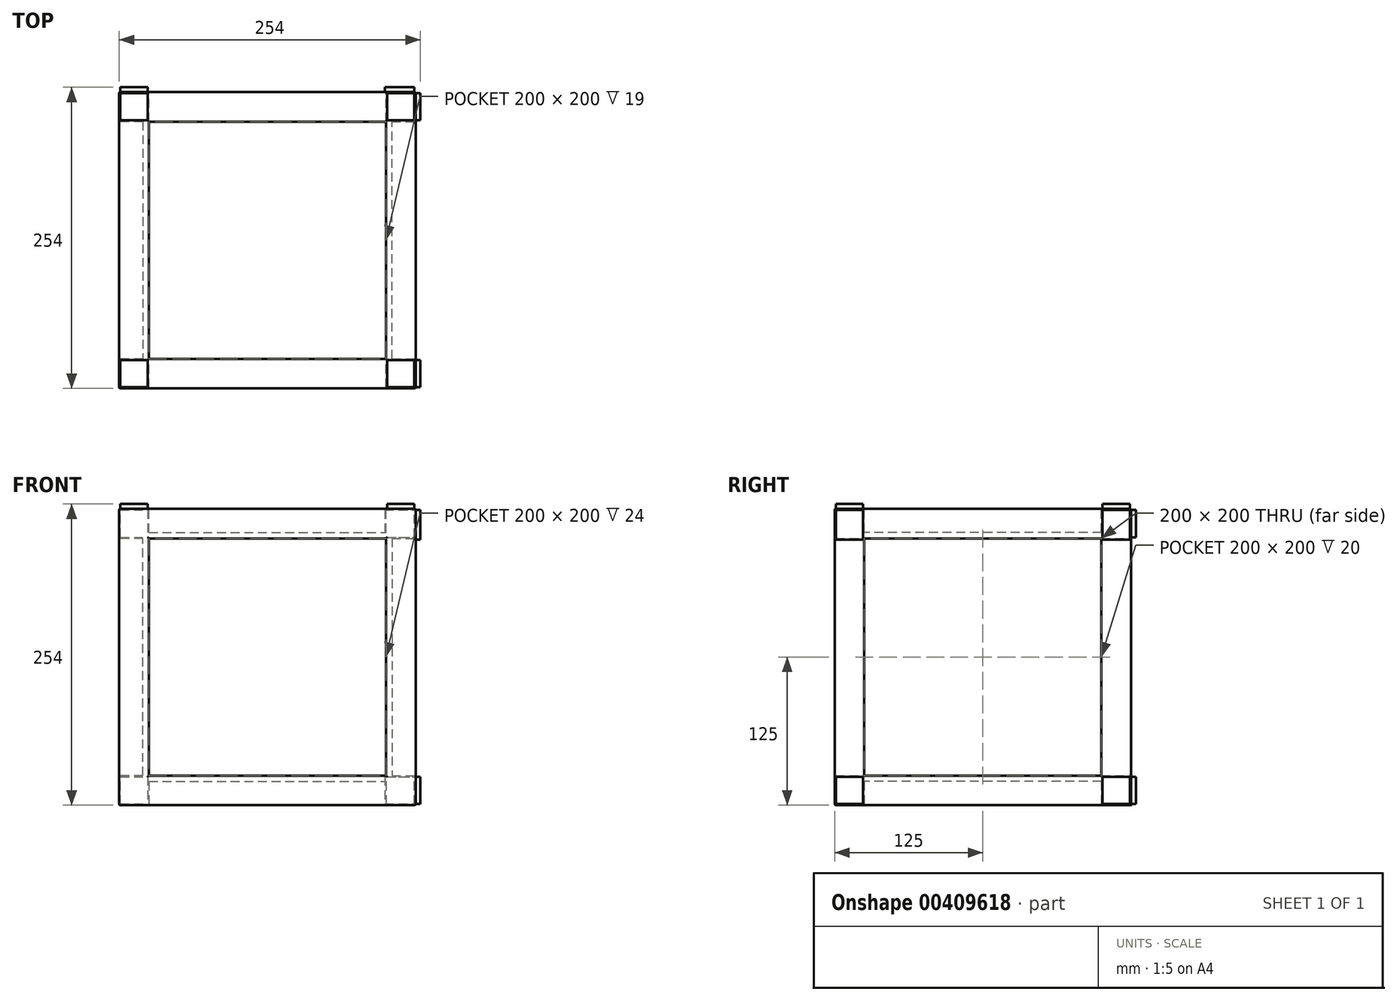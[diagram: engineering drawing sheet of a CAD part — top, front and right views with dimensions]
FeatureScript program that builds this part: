
annotation { "Feature Type Name" : "Feature", "Feature Type Description" : "" }
export const myFeature = defineFeature(function(context is Context, id is Id, definition is map)
    precondition{}
    {
        {
            var Q0;
            Q0=qCreatedBy(makeId("Front.planeOp"),FACE);
            var sketch = newSketch(context, id + "F0", { "sketchPlane" : qUnion([Q0])});
            skLineSegment(sketch, "E0.bottom", {"start": v(0, 0) * mm, "end": v(250, 0) * mm});
            skLineSegment(sketch, "E0.top", {"start": v(0, 250) * mm, "end": v(250, 250) * mm});
            skLineSegment(sketch, "E0.left", {"start": v(0, 0) * mm, "end": v(0, 250) * mm});
            skLineSegment(sketch, "E0.right", {"start": v(250, 0) * mm, "end": v(250, 250) * mm});
            skLineSegment(sketch, "E1.bottom", {"start": v(25, 225) * mm, "end": v(225, 225) * mm});
            skLineSegment(sketch, "E1.top", {"start": v(25, 25) * mm, "end": v(225, 25) * mm});
            skLineSegment(sketch, "E1.left", {"start": v(25, 225) * mm, "end": v(25, 25) * mm});
            skLineSegment(sketch, "E1.right", {"start": v(225, 225) * mm, "end": v(225, 25) * mm});
            skSolve(sketch);
        }
        {
            var Q0;
            Q0=makeQuery(id+"F0.imprint","IMPRINT",FACE,{"disambiguationData":[TD([[makeQuery(id+"F0.imprint","IMPRINT",EDGE,{"derivedFrom":sQuery(id+"F0.wireOp",EDGE,"E0.bottom")}),1.0]])]});
            extrude(context, id + "F1", {"entities" : qUnion([Q0]), "endBound" : BoundingType.SYMMETRIC, "depth" : 250 * mm});
        }
        {
            var Q0;
            Q0=qCreatedBy(makeId("Front.planeOp"),FACE);
            var sketch = newSketch(context, id + "F2", { "sketchPlane" : qUnion([Q0])});
            skLineSegment(sketch, "E2.bottom", {"start": v(25, 25) * mm, "end": v(225, 25) * mm});
            skLineSegment(sketch, "E2.top", {"start": v(25, 225) * mm, "end": v(225, 225) * mm});
            skLineSegment(sketch, "E2.left", {"start": v(25, 25) * mm, "end": v(25, 225) * mm});
            skLineSegment(sketch, "E2.right", {"start": v(225, 25) * mm, "end": v(225, 225) * mm});
            skSolve(sketch);
        }
        {
            var Q0;
            Q0=makeQuery(id+"F2.imprint","IMPRINT",FACE,{"disambiguationData":[TD([[makeQuery(id+"F2.imprint","IMPRINT",EDGE,{"derivedFrom":sQuery(id+"F2.wireOp",EDGE,"E2.bottom")}),1.0]])]});
            extrude(context, id + "F3", {"entities" : qUnion([Q0]), "operationType" : NewBodyOperationType.ADD, "endBound" : BoundingType.SYMMETRIC, "depth" : 200 * mm});
        }
        {
            var Q0;
            Q0=makeQuery(id+"F1.opExtrude","SWEPT_FACE",FACE,{"disambiguationData":[OSD([sQuery(id+"F0.wireOp",EDGE,"E0.left")])]});
            var sketch = newSketch(context, id + "F4", { "sketchPlane" : qUnion([Q0])});
            skLineSegment(sketch, "E3.bottom", {"start": v(-100, 25) * mm, "end": v(100, 25) * mm});
            skLineSegment(sketch, "E3.top", {"start": v(-100, 225) * mm, "end": v(100, 225) * mm});
            skLineSegment(sketch, "E3.left", {"start": v(-100, 25) * mm, "end": v(-100, 225) * mm});
            skLineSegment(sketch, "E3.right", {"start": v(100, 25) * mm, "end": v(100, 225) * mm});
            skSolve(sketch);
        }
        {
            var Q0;
            Q0=makeQuery(id+"F4.imprint","IMPRINT",FACE,{"disambiguationData":[TD([[makeQuery(id+"F4.imprint","IMPRINT",EDGE,{"derivedFrom":sQuery(id+"F4.wireOp",EDGE,"E3.bottom")}),1.0]])]});
            extrude(context, id + "F5", {"entities" : qUnion([Q0]), "operationType" : NewBodyOperationType.REMOVE, "oppositeDirection" : true, "depth" : 20 * mm});
        }
        {
            var Q0;
            Q0=makeQuery(id+"F1.opExtrude","SWEPT_FACE",FACE,{"disambiguationData":[OSD([sQuery(id+"F0.wireOp",EDGE,"E0.right")])]});
            var sketch = newSketch(context, id + "F6", { "sketchPlane" : qUnion([Q0])});
            skLineSegment(sketch, "E4.bottom", {"start": v(-100, 225) * mm, "end": v(100, 225) * mm});
            skLineSegment(sketch, "E4.top", {"start": v(-100, 25) * mm, "end": v(100, 25) * mm});
            skLineSegment(sketch, "E4.left", {"start": v(-100, 225) * mm, "end": v(-100, 25) * mm});
            skLineSegment(sketch, "E4.right", {"start": v(100, 225) * mm, "end": v(100, 25) * mm});
            skSolve(sketch);
        }
        {
            var Q0;
            Q0=makeQuery(id+"F6.imprint","IMPRINT",FACE,{"disambiguationData":[TD([[makeQuery(id+"F6.imprint","IMPRINT",EDGE,{"derivedFrom":sQuery(id+"F6.wireOp",EDGE,"E4.bottom")}),-1.0]])]});
            extrude(context, id + "F7", {"entities" : qUnion([Q0]), "operationType" : NewBodyOperationType.REMOVE, "oppositeDirection" : true, "depth" : 20 * mm});
        }
        {
            var Q0;
            Q0=qCreatedBy(makeId("Top.planeOp"),FACE);
            var sketch = newSketch(context, id + "F8", { "sketchPlane" : qUnion([Q0])});
            skLineSegment(sketch, "E5.bottom", {"start": v(25, 100) * mm, "end": v(225, 100) * mm});
            skLineSegment(sketch, "E5.top", {"start": v(25, -100) * mm, "end": v(225, -100) * mm});
            skLineSegment(sketch, "E5.left", {"start": v(25, 100) * mm, "end": v(25, -100) * mm});
            skLineSegment(sketch, "E5.right", {"start": v(225, 100) * mm, "end": v(225, -100) * mm});
            skSolve(sketch);
        }
        {
            var Q0;
            Q0=makeQuery(id+"F8.imprint","IMPRINT",FACE,{"disambiguationData":[TD([[makeQuery(id+"F8.imprint","IMPRINT",EDGE,{"derivedFrom":sQuery(id+"F8.wireOp",EDGE,"E5.bottom")}),-1.0]])]});
            extrude(context, id + "F9", {"entities" : qUnion([Q0]), "operationType" : NewBodyOperationType.REMOVE, "depth" : 20 * mm});
        }
        {
            var Q0;
            Q0=makeQuery(id+"F1.opExtrude","SWEPT_FACE",FACE,{"disambiguationData":[OSD([sQuery(id+"F0.wireOp",EDGE,"E0.top")])]});
            var sketch = newSketch(context, id + "F10", { "sketchPlane" : qUnion([Q0])});
            skLineSegment(sketch, "E6.bottom", {"start": v(25, 100) * mm, "end": v(225, 100) * mm});
            skLineSegment(sketch, "E6.top", {"start": v(25, -100) * mm, "end": v(225, -100) * mm});
            skLineSegment(sketch, "E6.left", {"start": v(25, 100) * mm, "end": v(25, -100) * mm});
            skLineSegment(sketch, "E6.right", {"start": v(225, 100) * mm, "end": v(225, -100) * mm});
            skSolve(sketch);
        }
        {
            var Q0;
            Q0=makeQuery(id+"F10.imprint","IMPRINT",FACE,{"disambiguationData":[TD([[makeQuery(id+"F10.imprint","IMPRINT",EDGE,{"derivedFrom":sQuery(id+"F10.wireOp",EDGE,"E6.bottom")}),-1.0]])]});
            extrude(context, id + "F11", {"entities" : qUnion([Q0]), "operationType" : NewBodyOperationType.REMOVE, "oppositeDirection" : true, "depth" : 20 * mm});
        }
        {
            var Q0;
            Q0=makeQuery(id+"F9.boolean.opBoolean","COPY",EDGE,{"derivedFrom":makeQuery(id+"F9.opExtrude","CAP_EDGE",EDGE,{"disambiguationData":[OSD([sQuery(id+"F8.wireOp",EDGE,"E5.left")])],"isStart":true})});
            var Q1;
            Q1=makeQuery(id+"F9.boolean.opBoolean","COPY",EDGE,{"derivedFrom":makeQuery(id+"F9.opExtrude","CAP_EDGE",EDGE,{"disambiguationData":[OSD([sQuery(id+"F8.wireOp",EDGE,"E5.top")])],"isStart":true})});
            var Q2;
            Q2=makeQuery(id+"F9.boolean.opBoolean","COPY",EDGE,{"derivedFrom":makeQuery(id+"F9.opExtrude","CAP_EDGE",EDGE,{"disambiguationData":[OSD([sQuery(id+"F8.wireOp",EDGE,"E5.bottom")])],"isStart":true})});
            var Q3;
            Q3=makeQuery(id+"F9.boolean.opBoolean","COPY",EDGE,{"derivedFrom":makeQuery(id+"F9.opExtrude","CAP_EDGE",EDGE,{"disambiguationData":[OSD([sQuery(id+"F8.wireOp",EDGE,"E5.right")])],"isStart":true})});
            var Q4;
            Q4=makeQuery(id+"F1.opExtrude","SWEPT_EDGE",EDGE,{"disambiguationData":[OSD([sQuery(id+"F0.wireOp",EDGE,"E0.bottom"),sQuery(id+"F0.wireOp",EDGE,"E0.right")])]});
            var Q5;
            Q5=makeQuery(id+"F7.boolean.opBoolean","COPY",EDGE,{"derivedFrom":makeQuery(id+"F7.opExtrude","CAP_EDGE",EDGE,{"disambiguationData":[OSD([sQuery(id+"F6.wireOp",EDGE,"E4.top")])],"isStart":true})});
            var Q6;
            Q6=makeQuery(id+"F7.boolean.opBoolean","COPY",EDGE,{"derivedFrom":makeQuery(id+"F7.opExtrude","CAP_EDGE",EDGE,{"disambiguationData":[OSD([sQuery(id+"F6.wireOp",EDGE,"E4.right")])],"isStart":true})});
            var Q7;
            Q7=makeQuery(id+"F7.boolean.opBoolean","COPY",EDGE,{"derivedFrom":makeQuery(id+"F7.opExtrude","CAP_EDGE",EDGE,{"disambiguationData":[OSD([sQuery(id+"F6.wireOp",EDGE,"E4.bottom")])],"isStart":true})});
            var Q8;
            Q8=makeQuery(id+"F7.boolean.opBoolean","COPY",EDGE,{"derivedFrom":makeQuery(id+"F7.opExtrude","CAP_EDGE",EDGE,{"disambiguationData":[OSD([sQuery(id+"F6.wireOp",EDGE,"E4.left")])],"isStart":true})});
            var Q9;
            Q9=makeQuery(id+"F1.opExtrude","CAP_EDGE",EDGE,{"disambiguationData":[OSD([sQuery(id+"F0.wireOp",EDGE,"E0.right")])],"isStart":false});
            var Q10;
            Q10=makeQuery(id+"F1.opExtrude","SWEPT_EDGE",EDGE,{"disambiguationData":[OSD([sQuery(id+"F0.wireOp",EDGE,"E0.top"),sQuery(id+"F0.wireOp",EDGE,"E0.right")])]});
            var Q11;
            Q11=makeQuery(id+"F1.opExtrude","CAP_EDGE",EDGE,{"disambiguationData":[OSD([sQuery(id+"F0.wireOp",EDGE,"E0.top")])],"isStart":true});
            var Q12;
            Q12=makeQuery(id+"F1.opExtrude","CAP_EDGE",EDGE,{"disambiguationData":[OSD([sQuery(id+"F0.wireOp",EDGE,"E0.right")])],"isStart":true});
            var Q13;
            Q13=makeQuery(id+"F1.opExtrude","CAP_EDGE",EDGE,{"disambiguationData":[OSD([sQuery(id+"F0.wireOp",EDGE,"E1.right")])],"isStart":true});
            var Q14;
            Q14=makeQuery(id+"F1.opExtrude","CAP_EDGE",EDGE,{"disambiguationData":[OSD([sQuery(id+"F0.wireOp",EDGE,"E1.bottom")])],"isStart":true});
            var Q15;
            Q15=makeQuery(id+"F1.opExtrude","CAP_EDGE",EDGE,{"disambiguationData":[OSD([sQuery(id+"F0.wireOp",EDGE,"E1.left")])],"isStart":true});
            var Q16;
            Q16=makeQuery(id+"F1.opExtrude","CAP_EDGE",EDGE,{"disambiguationData":[OSD([sQuery(id+"F0.wireOp",EDGE,"E1.top")])],"isStart":true});
            var Q17;
            Q17=makeQuery(id+"F5.boolean.opBoolean","COPY",EDGE,{"derivedFrom":makeQuery(id+"F5.opExtrude","CAP_EDGE",EDGE,{"disambiguationData":[OSD([sQuery(id+"F4.wireOp",EDGE,"E3.left")])],"isStart":true})});
            var Q18;
            Q18=makeQuery(id+"F5.boolean.opBoolean","COPY",EDGE,{"derivedFrom":makeQuery(id+"F5.opExtrude","CAP_EDGE",EDGE,{"disambiguationData":[OSD([sQuery(id+"F4.wireOp",EDGE,"E3.bottom")])],"isStart":true})});
            var Q19;
            Q19=makeQuery(id+"F1.opExtrude","CAP_EDGE",EDGE,{"disambiguationData":[OSD([sQuery(id+"F0.wireOp",EDGE,"E0.left")])],"isStart":true});
            var Q20;
            Q20=makeQuery(id+"F1.opExtrude","SWEPT_EDGE",EDGE,{"disambiguationData":[OSD([sQuery(id+"F0.wireOp",EDGE,"E0.bottom"),sQuery(id+"F0.wireOp",EDGE,"E0.left")])]});
            var Q21;
            Q21=makeQuery(id+"F1.opExtrude","CAP_EDGE",EDGE,{"disambiguationData":[OSD([sQuery(id+"F0.wireOp",EDGE,"E0.left")])],"isStart":false});
            var Q22;
            Q22=makeQuery(id+"F1.opExtrude","SWEPT_EDGE",EDGE,{"disambiguationData":[OSD([sQuery(id+"F0.wireOp",EDGE,"E0.top"),sQuery(id+"F0.wireOp",EDGE,"E0.left")])]});
            var Q23;
            Q23=makeQuery(id+"F5.boolean.opBoolean","COPY",EDGE,{"derivedFrom":makeQuery(id+"F5.opExtrude","CAP_EDGE",EDGE,{"disambiguationData":[OSD([sQuery(id+"F4.wireOp",EDGE,"E3.top")])],"isStart":true})});
            var Q24;
            Q24=makeQuery(id+"F5.boolean.opBoolean","COPY",EDGE,{"derivedFrom":makeQuery(id+"F5.opExtrude","CAP_EDGE",EDGE,{"disambiguationData":[OSD([sQuery(id+"F4.wireOp",EDGE,"E3.right")])],"isStart":true})});
            var Q25;
            Q25=makeQuery(id+"F1.opExtrude","CAP_EDGE",EDGE,{"disambiguationData":[OSD([sQuery(id+"F0.wireOp",EDGE,"E0.top")])],"isStart":false});
            var Q26;
            Q26=makeQuery(id+"F1.opExtrude","CAP_FACE",FACE,{"disambiguationData":[OSD([sQuery(id+"F0.wireOp",EDGE,"E0.bottom"),sQuery(id+"F0.wireOp",EDGE,"E0.top"),sQuery(id+"F0.wireOp",EDGE,"E0.left"),sQuery(id+"F0.wireOp",EDGE,"E0.right"),sQuery(id+"F0.wireOp",EDGE,"E1.bottom"),sQuery(id+"F0.wireOp",EDGE,"E1.top"),sQuery(id+"F0.wireOp",EDGE,"E1.left"),sQuery(id+"F0.wireOp",EDGE,"E1.right")])],"isStart":false});
            var Q27;
            Q27=makeQuery(id+"F1.opExtrude","SWEPT_FACE",FACE,{"disambiguationData":[OSD([sQuery(id+"F0.wireOp",EDGE,"E0.top")])]});
            fillet(context, id + "F12", {"entities" : qUnion([Q0, Q1, Q2, Q3, Q4, Q5, Q6, Q7, Q8, Q9, Q10, Q11, Q12, Q13, Q14, Q15, Q16, Q17, Q18, Q19, Q20, Q21, Q22, Q23, Q24, Q25, Q26, Q27]), "radius" : 1 * mm, "tangentPropagation" : true, "allowEdgeOverflow" : false});
        }
        {
            var Q0;
            Q0=makeQuery(id+"F1.opExtrude","SWEPT_FACE",FACE,{"disambiguationData":[OSD([sQuery(id+"F0.wireOp",EDGE,"E0.top")])]});
            var sketch = newSketch(context, id + "F13", { "sketchPlane" : qUnion([Q0])});
            skLineSegment(sketch, "E7.bottom", {"start": v(249, 124) * mm, "end": v(226, 124) * mm});
            skLineSegment(sketch, "E7.top", {"start": v(249, 101) * mm, "end": v(226, 101) * mm});
            skLineSegment(sketch, "E7.left", {"start": v(249, 124) * mm, "end": v(249, 101) * mm});
            skLineSegment(sketch, "E7.right", {"start": v(226, 124) * mm, "end": v(226, 101) * mm});
            skLineSegment(sketch, "E8.0.1.0", {"start": v(249, -101) * mm, "end": v(249, -124) * mm});
            skLineSegment(sketch, "E8.0.1.1", {"start": v(249, -124) * mm, "end": v(226, -124) * mm});
            skLineSegment(sketch, "E8.0.1.2", {"start": v(226, -101) * mm, "end": v(226, -124) * mm});
            skLineSegment(sketch, "E8.0.1.3", {"start": v(249, -101) * mm, "end": v(226, -101) * mm});
            skLineSegment(sketch, "E8.1.0.0", {"start": v(24, 124) * mm, "end": v(24, 101) * mm});
            skLineSegment(sketch, "E8.1.0.1", {"start": v(24, 101) * mm, "end": v(1, 101) * mm});
            skLineSegment(sketch, "E8.1.0.2", {"start": v(1, 124) * mm, "end": v(1, 101) * mm});
            skLineSegment(sketch, "E8.1.0.3", {"start": v(24, 124) * mm, "end": v(1, 124) * mm});
            skLineSegment(sketch, "E8.1.1.0", {"start": v(24, -101) * mm, "end": v(24, -124) * mm});
            skLineSegment(sketch, "E8.1.1.1", {"start": v(24, -124) * mm, "end": v(1, -124) * mm});
            skLineSegment(sketch, "E8.1.1.2", {"start": v(1, -101) * mm, "end": v(1, -124) * mm});
            skLineSegment(sketch, "E8.1.1.3", {"start": v(24, -101) * mm, "end": v(1, -101) * mm});
            skLineSegment(sketch, "E8.direction1", {"start": v(249, 101) * mm, "end": v(24, 101) * mm, "construction": true});
            skLineSegment(sketch, "E8.direction2", {"start": v(249, 101) * mm, "end": v(249, -124) * mm, "construction": true});
            skSolve(sketch);
        }
        {
            var Q0;
            Q0=makeQuery(id+"F13.imprint","IMPRINT",FACE,{"disambiguationData":[TD([[makeQuery(id+"F13.imprint","IMPRINT",EDGE,{"derivedFrom":sQuery(id+"F13.wireOp",EDGE,"E7.bottom")}),1.0]])]});
            var Q1;
            Q1=makeQuery(id+"F13.imprint","IMPRINT",FACE,{"disambiguationData":[TD([[makeQuery(id+"F13.imprint","IMPRINT",EDGE,{"derivedFrom":sQuery(id+"F13.wireOp",EDGE,"E8.0.1.0")}),1.0]])]});
            var Q2;
            Q2=makeQuery(id+"F13.imprint","IMPRINT",FACE,{"disambiguationData":[TD([[makeQuery(id+"F13.imprint","IMPRINT",EDGE,{"derivedFrom":sQuery(id+"F13.wireOp",EDGE,"E8.1.1.0")}),-1.0]])]});
            var Q3;
            Q3=makeQuery(id+"F13.imprint","IMPRINT",FACE,{"disambiguationData":[TD([[makeQuery(id+"F13.imprint","IMPRINT",EDGE,{"derivedFrom":sQuery(id+"F13.wireOp",EDGE,"E8.1.0.0")}),-1.0]])]});
            extrude(context, id + "F14", {"entities" : qUnion([Q0, Q1, Q2, Q3]), "operationType" : NewBodyOperationType.ADD, "depth" : 4 * mm});
        }
        {
            var Q0;
            Q0=makeQuery(id+"F1.opExtrude","SWEPT_FACE",FACE,{"disambiguationData":[OSD([sQuery(id+"F0.wireOp",EDGE,"E0.right")])]});
            var sketch = newSketch(context, id + "F15", { "sketchPlane" : qUnion([Q0])});
            skLineSegment(sketch, "E9.bottom", {"start": v(124, 249) * mm, "end": v(101, 249) * mm});
            skLineSegment(sketch, "E9.top", {"start": v(124, 224) * mm, "end": v(101, 224) * mm});
            skLineSegment(sketch, "E9.left", {"start": v(124, 249) * mm, "end": v(124, 224) * mm});
            skLineSegment(sketch, "E9.right", {"start": v(101, 249) * mm, "end": v(101, 224) * mm});
            skLineSegment(sketch, "E10.0.1.0", {"start": v(124, 24) * mm, "end": v(124, -1) * mm});
            skLineSegment(sketch, "E10.0.1.1", {"start": v(124, -1) * mm, "end": v(101, -1) * mm});
            skLineSegment(sketch, "E10.0.1.2", {"start": v(101, 24) * mm, "end": v(101, -1) * mm});
            skLineSegment(sketch, "E10.0.1.3", {"start": v(124, 24) * mm, "end": v(101, 24) * mm});
            skLineSegment(sketch, "E10.1.0.0", {"start": v(-101, 249) * mm, "end": v(-101, 224) * mm});
            skLineSegment(sketch, "E10.1.0.1", {"start": v(-101, 224) * mm, "end": v(-124, 224) * mm});
            skLineSegment(sketch, "E10.1.0.2", {"start": v(-124, 249) * mm, "end": v(-124, 224) * mm});
            skLineSegment(sketch, "E10.1.0.3", {"start": v(-101, 249) * mm, "end": v(-124, 249) * mm});
            skLineSegment(sketch, "E10.1.1.0", {"start": v(-101, 24) * mm, "end": v(-101, -1) * mm});
            skLineSegment(sketch, "E10.1.1.1", {"start": v(-101, -1) * mm, "end": v(-124, -1) * mm});
            skLineSegment(sketch, "E10.1.1.2", {"start": v(-124, 24) * mm, "end": v(-124, -1) * mm});
            skLineSegment(sketch, "E10.1.1.3", {"start": v(-101, 24) * mm, "end": v(-124, 24) * mm});
            skLineSegment(sketch, "E10.direction1", {"start": v(124, 224) * mm, "end": v(-101, 224) * mm, "construction": true});
            skLineSegment(sketch, "E10.direction2", {"start": v(124, 224) * mm, "end": v(124, -1) * mm, "construction": true});
            skSolve(sketch);
        }
        {
            var Q0;
            {var subQ5=sQuery(id+"F15.wireOp",EDGE,"E9.bottom");Q0=makeQuery(id+"F15.imprint","IMPRINT",FACE,{"disambiguationData":[TD([[makeQuery(id+"F15.imprint","IMPRINT",EDGE,{"derivedFrom":subQ5}),1.0]])]});}
            var Q1;
            {var subQ0=sQuery(id+"F15.wireOp",EDGE,"E10.1.0.1");Q1=makeQuery(id+"F15.imprint","IMPRINT",FACE,{"disambiguationData":[TD([[makeQuery(id+"F15.imprint","IMPRINT",EDGE,{"derivedFrom":subQ0}),-1.0]])]});}
            var Q2;
            {var subQ0=sQuery(id+"F15.wireOp",EDGE,"E10.1.1.3");Q2=makeQuery(id+"F15.imprint","IMPRINT",FACE,{"disambiguationData":[TD([[makeQuery(id+"F15.imprint","IMPRINT",EDGE,{"derivedFrom":subQ0}),1.0]])]});}
            var Q3;
            {var subQ5=sQuery(id+"F15.wireOp",EDGE,"E10.0.1.3");Q3=makeQuery(id+"F15.imprint","IMPRINT",FACE,{"disambiguationData":[TD([[makeQuery(id+"F15.imprint","IMPRINT",EDGE,{"derivedFrom":subQ5}),1.0]])]});}
            extrude(context, id + "F16", {"entities" : qUnion([Q0, Q1, Q2, Q3]), "operationType" : NewBodyOperationType.ADD, "depth" : 4 * mm});
        }
        {
            var Q0;
            Q0=makeQuery(id+"F1.opExtrude","CAP_FACE",FACE,{"disambiguationData":[OSD([sQuery(id+"F0.wireOp",EDGE,"E0.bottom"),sQuery(id+"F0.wireOp",EDGE,"E0.top"),sQuery(id+"F0.wireOp",EDGE,"E0.left"),sQuery(id+"F0.wireOp",EDGE,"E0.right"),sQuery(id+"F0.wireOp",EDGE,"E1.bottom"),sQuery(id+"F0.wireOp",EDGE,"E1.top"),sQuery(id+"F0.wireOp",EDGE,"E1.left"),sQuery(id+"F0.wireOp",EDGE,"E1.right")])],"isStart":true});
            var sketch = newSketch(context, id + "F17", { "sketchPlane" : qUnion([Q0])});
            skLineSegment(sketch, "E11.bottom", {"start": v(1, 249) * mm, "end": v(-24, 249) * mm});
            skLineSegment(sketch, "E11.top", {"start": v(1, 226) * mm, "end": v(-24, 226) * mm});
            skLineSegment(sketch, "E11.left", {"start": v(1, 249) * mm, "end": v(1, 226) * mm});
            skLineSegment(sketch, "E11.right", {"start": v(-24, 249) * mm, "end": v(-24, 226) * mm});
            skLineSegment(sketch, "E12.0.1.0", {"start": v(1, 24) * mm, "end": v(1, 1) * mm});
            skLineSegment(sketch, "E12.0.1.1", {"start": v(1, 1) * mm, "end": v(-24, 1) * mm});
            skLineSegment(sketch, "E12.0.1.2", {"start": v(-24, 24) * mm, "end": v(-24, 1) * mm});
            skLineSegment(sketch, "E12.0.1.3", {"start": v(1, 24) * mm, "end": v(-24, 24) * mm});
            skLineSegment(sketch, "E12.1.0.0", {"start": v(-224, 249) * mm, "end": v(-224, 226) * mm});
            skLineSegment(sketch, "E12.1.0.1", {"start": v(-224, 226) * mm, "end": v(-249, 226) * mm});
            skLineSegment(sketch, "E12.1.0.2", {"start": v(-249, 249) * mm, "end": v(-249, 226) * mm});
            skLineSegment(sketch, "E12.1.0.3", {"start": v(-224, 249) * mm, "end": v(-249, 249) * mm});
            skLineSegment(sketch, "E12.1.1.0", {"start": v(-224, 24) * mm, "end": v(-224, 1) * mm});
            skLineSegment(sketch, "E12.1.1.1", {"start": v(-224, 1) * mm, "end": v(-249, 1) * mm});
            skLineSegment(sketch, "E12.1.1.2", {"start": v(-249, 24) * mm, "end": v(-249, 1) * mm});
            skLineSegment(sketch, "E12.1.1.3", {"start": v(-224, 24) * mm, "end": v(-249, 24) * mm});
            skLineSegment(sketch, "E12.direction1", {"start": v(1, 226) * mm, "end": v(-224, 226) * mm, "construction": true});
            skLineSegment(sketch, "E12.direction2", {"start": v(1, 226) * mm, "end": v(1, 1) * mm, "construction": true});
            skSolve(sketch);
        }
        {
            var Q0;
            {var subQ0=sQuery(id+"F17.wireOp",EDGE,"E12.0.1.2");Q0=makeQuery(id+"F17.imprint","IMPRINT",FACE,{"disambiguationData":[TD([[makeQuery(id+"F17.imprint","IMPRINT",EDGE,{"derivedFrom":subQ0}),1.0]])]});}
            var Q1;
            {var subQ6=sQuery(id+"F17.wireOp",EDGE,"E12.1.1.0");Q1=makeQuery(id+"F17.imprint","IMPRINT",FACE,{"disambiguationData":[TD([[makeQuery(id+"F17.imprint","IMPRINT",EDGE,{"derivedFrom":subQ6}),-1.0]])]});}
            var Q2;
            {var subQ7=sQuery(id+"F17.wireOp",EDGE,"E12.1.0.0");Q2=makeQuery(id+"F17.imprint","IMPRINT",FACE,{"disambiguationData":[TD([[makeQuery(id+"F17.imprint","IMPRINT",EDGE,{"derivedFrom":subQ7}),-1.0]])]});}
            var Q3;
            {var subQ8=sQuery(id+"F17.wireOp",EDGE,"E11.right");Q3=makeQuery(id+"F17.imprint","IMPRINT",FACE,{"disambiguationData":[TD([[makeQuery(id+"F17.imprint","IMPRINT",EDGE,{"derivedFrom":subQ8}),1.0]])]});}
            extrude(context, id + "F18", {"entities" : qUnion([Q0, Q1, Q2, Q3]), "operationType" : NewBodyOperationType.ADD, "depth" : 4 * mm});
        }
    });
